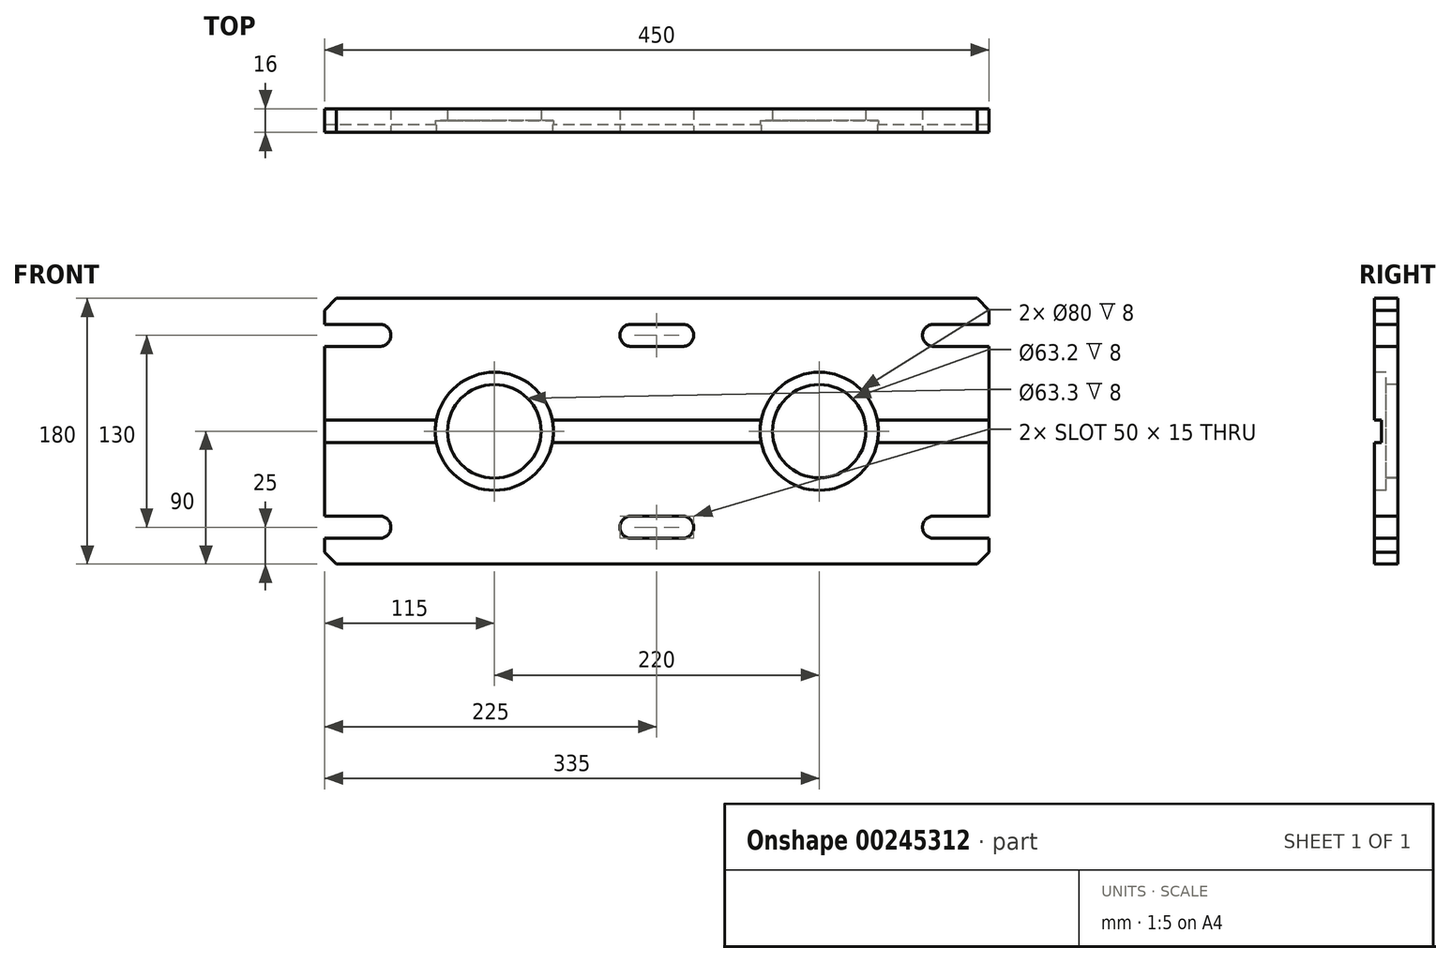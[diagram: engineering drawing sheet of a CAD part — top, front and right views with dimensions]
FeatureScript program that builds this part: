
annotation { "Feature Type Name" : "Feature", "Feature Type Description" : "" }
export const myFeature = defineFeature(function(context is Context, id is Id, definition is map)
    precondition{}
    {
        {
            var Q0;
            Q0=qCreatedBy(makeId("Front.planeOp"),FACE);
            var sketch = newSketch(context, id + "F0", { "sketchPlane" : qUnion([Q0])});
            skLineSegment(sketch, "E0.bottom", {"start": v(0, 0) * mm, "end": v(450, 0) * mm});
            skLineSegment(sketch, "E0.top", {"start": v(0, 180) * mm, "end": v(450, 180) * mm});
            skLineSegment(sketch, "E0.left", {"start": v(0, 0) * mm, "end": v(0, 180) * mm});
            skLineSegment(sketch, "E0.right", {"start": v(450, 0) * mm, "end": v(450, 180) * mm});
            skSolve(sketch);
        }
        {
            var Q0;
            Q0 = qSketchRegion(id + "F0", true);
            extrude(context, id + "F1", {"entities" : qUnion([Q0]), "depth" : 16 * mm, "offsetDistance" : 25 * mm});
        }
        {
            var Q0;
            Q0=makeQuery(id+"F1.opExtrude","SWEPT_EDGE",EDGE,{"disambiguationData":[OSD([sQuery(id+"F0.wireOp",EDGE,"E0.top"),sQuery(id+"F0.wireOp",EDGE,"E0.right")])]});
            var Q1;
            Q1=makeQuery(id+"F1.opExtrude","SWEPT_EDGE",EDGE,{"disambiguationData":[OSD([sQuery(id+"F0.wireOp",EDGE,"E0.bottom"),sQuery(id+"F0.wireOp",EDGE,"E0.right")])]});
            var Q2;
            Q2=makeQuery(id+"F1.opExtrude","SWEPT_EDGE",EDGE,{"disambiguationData":[OSD([sQuery(id+"F0.wireOp",EDGE,"E0.top"),sQuery(id+"F0.wireOp",EDGE,"E0.left")])]});
            var Q3;
            Q3=makeQuery(id+"F1.opExtrude","SWEPT_EDGE",EDGE,{"disambiguationData":[OSD([sQuery(id+"F0.wireOp",EDGE,"E0.bottom"),sQuery(id+"F0.wireOp",EDGE,"E0.left")])]});
            chamfer(context, id + "F2", {"entities" : qUnion([Q0, Q1, Q2, Q3]), "width" : 8 * mm, "tangentPropagation" : true});
        }
        {
            var Q0;
            Q0=makeQuery(id+"F1.opExtrude","CAP_FACE",FACE,{"disambiguationData":[OSD([sQuery(id+"F0.wireOp",EDGE,"E0.bottom"),sQuery(id+"F0.wireOp",EDGE,"E0.top"),sQuery(id+"F0.wireOp",EDGE,"E0.left"),sQuery(id+"F0.wireOp",EDGE,"E0.right")])],"isStart":false});
            var sketch = newSketch(context, id + "F3", { "sketchPlane" : qUnion([Q0])});
            skCircle(sketch, "E1", {"center": v(335, 90) * mm, "radius": 31.6 * mm});
            skPoint(sketch, "E1.centerSnap0", {"position": v(450, 90) * mm});
            skCircle(sketch, "E2", {"center": v(115, 90) * mm, "radius": 31.65 * mm});
            skPoint(sketch, "E2.centerSnap0", {"position": v(0, 90) * mm});
            skSolve(sketch);
        }
        {
            var Q0;
            Q0=makeQuery(id+"F3.imprint","IMPRINT",FACE,{"disambiguationData":[TD([[makeQuery(id+"F3.imprint","IMPRINT",EDGE,{"derivedFrom":sQuery(id+"F3.wireOp",EDGE,"E1")}),1.0]])]});
            var Q1;
            Q1=makeQuery(id+"F3.imprint","IMPRINT",FACE,{"disambiguationData":[TD([[makeQuery(id+"F3.imprint","IMPRINT",EDGE,{"derivedFrom":sQuery(id+"F3.wireOp",EDGE,"E2")}),1.0]])]});
            extrude(context, id + "F4", {"entities" : qUnion([Q0, Q1]), "operationType" : NewBodyOperationType.REMOVE, "endBound" : BoundingType.THROUGH_ALL, "oppositeDirection" : true, "depth" : 25 * mm, "offsetDistance" : 25 * mm});
        }
        {
            var Q0;
            Q0=makeQuery(id+"F1.opExtrude","CAP_FACE",FACE,{"disambiguationData":[OSD([sQuery(id+"F0.wireOp",EDGE,"E0.bottom"),sQuery(id+"F0.wireOp",EDGE,"E0.top"),sQuery(id+"F0.wireOp",EDGE,"E0.left"),sQuery(id+"F0.wireOp",EDGE,"E0.right")])],"isStart":false});
            var sketch = newSketch(context, id + "F5", { "sketchPlane" : qUnion([Q0])});
            skLineSegment(sketch, "E3.bottom", {"start": v(242.5, 147.5) * mm, "end": v(207.5, 147.5) * mm});
            skLineSegment(sketch, "E3.top", {"start": v(242.5, 162.5) * mm, "end": v(207.5, 162.5) * mm});
            skLineSegment(sketch, "E3.left", {"start": v(250, 155) * mm, "end": v(250, 155) * mm});
            skLineSegment(sketch, "E3.right", {"start": v(200, 155) * mm, "end": v(200, 155) * mm});
            skPoint(sketch, "E3.middle", {"position": v(225, 155) * mm});
            skPoint(sketch, "E3.middle.positionSnap0", {"position": v(225, 180) * mm});
            skPoint(sketch, "E3.centerSnap0", {"position": v(225, 180) * mm});
            skPoint(sketch, "E4.visualSharp", {"position": v(200, 162.5) * mm});
            skArc(sketch, "E4.filletArc", {"start": v(207.5, 162.5) * mm, "mid": v(202.2, 160.3) * mm, "end": v(200, 155) * mm});
            skPoint(sketch, "E5.visualSharp", {"position": v(200, 147.5) * mm});
            skArc(sketch, "E5.filletArc", {"start": v(200, 155) * mm, "mid": v(202.2, 149.7) * mm, "end": v(207.5, 147.5) * mm});
            skPoint(sketch, "E6.visualSharp", {"position": v(250, 147.5) * mm});
            skArc(sketch, "E6.filletArc", {"start": v(242.5, 147.5) * mm, "mid": v(247.8, 149.7) * mm, "end": v(250, 155) * mm});
            skPoint(sketch, "E7.visualSharp", {"position": v(250, 162.5) * mm});
            skArc(sketch, "E7.filletArc", {"start": v(250, 155) * mm, "mid": v(247.8, 160.3) * mm, "end": v(242.5, 162.5) * mm});
            skLineSegment(sketch, "E8.bottom", {"start": v(37.5, 147.5) * mm, "end": v(-68.92, 147.5) * mm});
            skLineSegment(sketch, "E8.top", {"start": v(37.5, 162.5) * mm, "end": v(-68.92, 162.5) * mm});
            skLineSegment(sketch, "E8.left", {"start": v(45, 155) * mm, "end": v(45, 155) * mm});
            skLineSegment(sketch, "E8.right", {"start": v(-68.92, 147.5) * mm, "end": v(-68.92, 162.5) * mm});
            skPoint(sketch, "E8.middle", {"position": v(-11.96, 155) * mm});
            skLineSegment(sketch, "E9.bottom", {"start": v(455.82, 162.5) * mm, "end": v(412.5, 162.5) * mm});
            skLineSegment(sketch, "E9.top", {"start": v(455.82, 147.5) * mm, "end": v(412.5, 147.5) * mm});
            skLineSegment(sketch, "E9.left", {"start": v(455.82, 162.5) * mm, "end": v(455.82, 147.5) * mm});
            skLineSegment(sketch, "E9.right", {"start": v(405, 155) * mm, "end": v(405, 155) * mm});
            skPoint(sketch, "E9.middle", {"position": v(430.4, 155) * mm});
            skPoint(sketch, "E10.visualSharp", {"position": v(45, 162.5) * mm});
            skArc(sketch, "E10.filletArc", {"start": v(45, 155) * mm, "mid": v(42.8, 160.3) * mm, "end": v(37.5, 162.5) * mm});
            skPoint(sketch, "E11.visualSharp", {"position": v(45, 147.5) * mm});
            skArc(sketch, "E11.filletArc", {"start": v(37.5, 147.5) * mm, "mid": v(42.8, 149.7) * mm, "end": v(45, 155) * mm});
            skPoint(sketch, "E12.visualSharp", {"position": v(405, 162.5) * mm});
            skArc(sketch, "E12.filletArc", {"start": v(412.5, 162.5) * mm, "mid": v(407.2, 160.3) * mm, "end": v(405, 155) * mm});
            skPoint(sketch, "E13.visualSharp", {"position": v(405, 147.5) * mm});
            skArc(sketch, "E13.filletArc", {"start": v(405, 155) * mm, "mid": v(407.2, 149.7) * mm, "end": v(412.5, 147.5) * mm});
            skLineSegment(sketch, "E14", {"start": v(0, 90) * mm, "end": v(450, 90) * mm, "construction": true});
            skArc(sketch, "E15.MirrorCS", {"start": v(200, 25) * mm, "mid": v(202.2, 30.3) * mm, "end": v(207.5, 32.5) * mm});
            skArc(sketch, "E16.MirrorCS", {"start": v(405, 25) * mm, "mid": v(407.2, 30.3) * mm, "end": v(412.5, 32.5) * mm});
            skArc(sketch, "E17.MirrorCS", {"start": v(45, 25) * mm, "mid": v(42.8, 19.7) * mm, "end": v(37.5, 17.5) * mm});
            skLineSegment(sketch, "E18.MirrorCS", {"start": v(455.82, 17.5) * mm, "end": v(455.82, 32.5) * mm});
            skLineSegment(sketch, "E19.MirrorCS", {"start": v(-68.92, 32.5) * mm, "end": v(-68.92, 17.5) * mm});
            skArc(sketch, "E20.MirrorCS", {"start": v(250, 25) * mm, "mid": v(247.8, 19.7) * mm, "end": v(242.5, 17.5) * mm});
            skArc(sketch, "E21.MirrorCS", {"start": v(242.5, 32.5) * mm, "mid": v(247.8, 30.3) * mm, "end": v(250, 25) * mm});
            skArc(sketch, "E22.MirrorCS", {"start": v(207.5, 17.5) * mm, "mid": v(202.2, 19.7) * mm, "end": v(200, 25) * mm});
            skArc(sketch, "E23.MirrorCS", {"start": v(412.5, 17.5) * mm, "mid": v(407.2, 19.7) * mm, "end": v(405, 25) * mm});
            skArc(sketch, "E24.MirrorCS", {"start": v(37.5, 32.5) * mm, "mid": v(42.8, 30.3) * mm, "end": v(45, 25) * mm});
            skLineSegment(sketch, "E25.MirrorCS", {"start": v(242.5, 17.5) * mm, "end": v(207.5, 17.5) * mm});
            skLineSegment(sketch, "E26.MirrorCS", {"start": v(242.5, 32.5) * mm, "end": v(207.5, 32.5) * mm});
            skPoint(sketch, "E27.MirrorP", {"position": v(225, 0) * mm});
            skLineSegment(sketch, "E28.MirrorCS", {"start": v(455.82, 32.5) * mm, "end": v(412.5, 32.5) * mm});
            skLineSegment(sketch, "E29.MirrorCS", {"start": v(455.82, 17.5) * mm, "end": v(412.5, 17.5) * mm});
            skLineSegment(sketch, "E30.MirrorCS", {"start": v(37.5, 17.5) * mm, "end": v(-68.92, 17.5) * mm});
            skPoint(sketch, "E31.MirrorP", {"position": v(225, 25) * mm});
            skLineSegment(sketch, "E32.MirrorCS", {"start": v(37.5, 32.5) * mm, "end": v(-68.92, 32.5) * mm});
            skPoint(sketch, "E33.MirrorP", {"position": v(45, 17.5) * mm});
            skLineSegment(sketch, "E34.MirrorCS", {"start": v(200, 25) * mm, "end": v(200, 25) * mm});
            skPoint(sketch, "E35.MirrorP", {"position": v(45, 32.5) * mm});
            skPoint(sketch, "E36.MirrorP", {"position": v(200, 17.5) * mm});
            skPoint(sketch, "E37.MirrorP", {"position": v(405, 32.5) * mm});
            skPoint(sketch, "E38.MirrorP", {"position": v(430.4, 25) * mm});
            skPoint(sketch, "E39.MirrorP", {"position": v(250, 17.5) * mm});
            skLineSegment(sketch, "E40.MirrorCS", {"start": v(250, 25) * mm, "end": v(250, 25) * mm});
            skPoint(sketch, "E41.MirrorP", {"position": v(200, 32.5) * mm});
            skPoint(sketch, "E42.MirrorP", {"position": v(-11.96, 25) * mm});
            skPoint(sketch, "E43.MirrorP", {"position": v(405, 17.5) * mm});
            skLineSegment(sketch, "E44.MirrorCS", {"start": v(405, 25) * mm, "end": v(405, 25) * mm});
            skLineSegment(sketch, "E45.MirrorCS", {"start": v(45, 25) * mm, "end": v(45, 25) * mm});
            skPoint(sketch, "E46.MirrorP", {"position": v(250, 32.5) * mm});
            skSolve(sketch);
        }
        {
            var Q0;
            Q0 = qSketchRegion(id + "F5", true);
            extrude(context, id + "F6", {"entities" : qUnion([Q0]), "operationType" : NewBodyOperationType.REMOVE, "endBound" : BoundingType.THROUGH_ALL, "oppositeDirection" : true, "depth" : 25 * mm, "offsetDistance" : 25 * mm});
        }
        {
            var Q0;
            Q0=makeQuery(id+"F1.opExtrude","CAP_FACE",FACE,{"disambiguationData":[OSD([sQuery(id+"F0.wireOp",EDGE,"E0.bottom"),sQuery(id+"F0.wireOp",EDGE,"E0.top"),sQuery(id+"F0.wireOp",EDGE,"E0.left"),sQuery(id+"F0.wireOp",EDGE,"E0.right")])],"isStart":false});
            var sketch = newSketch(context, id + "F7", { "sketchPlane" : qUnion([Q0])});
            skCircle(sketch, "E47", {"center": v(115, 90) * mm, "radius": 40 * mm});
            skSolve(sketch);
        }
        {
            var Q0;
            Q0=makeQuery(id+"F7.imprint","IMPRINT",FACE,{"disambiguationData":[TD([[makeQuery(id+"F7.imprint","IMPRINT",EDGE,{"derivedFrom":sQuery(id+"F7.wireOp",EDGE,"E47")}),1.0]])]});
            extrude(context, id + "F8", {"entities" : qUnion([Q0]), "operationType" : NewBodyOperationType.REMOVE, "oppositeDirection" : true, "depth" : 8 * mm, "offsetDistance" : 25 * mm});
        }
        {
            var Q0;
            Q0=makeQuery(id+"F1.opExtrude","CAP_FACE",FACE,{"disambiguationData":[OSD([sQuery(id+"F0.wireOp",EDGE,"E0.bottom"),sQuery(id+"F0.wireOp",EDGE,"E0.top"),sQuery(id+"F0.wireOp",EDGE,"E0.left"),sQuery(id+"F0.wireOp",EDGE,"E0.right")])],"isStart":false});
            var sketch = newSketch(context, id + "F9", { "sketchPlane" : qUnion([Q0])});
            skCircle(sketch, "E48", {"center": v(335, 90) * mm, "radius": 40 * mm});
            skSolve(sketch);
        }
        {
            var Q0;
            Q0 = qSketchRegion(id + "F9", true);
            extrude(context, id + "F10", {"entities" : qUnion([Q0]), "operationType" : NewBodyOperationType.REMOVE, "oppositeDirection" : true, "depth" : 8 * mm, "offsetDistance" : 25 * mm});
        }
        {
            var Q0;
            {var subQ1=sQuery(id+"F0.wireOp",EDGE,"E0.left");Q0=makeQuery(id+"F6.boolean.opBoolean","SPLIT",FACE,{"disambiguationData":[TD([makeQuery(id+"F6.opExtrude","SWEPT_FACE",FACE,{"disambiguationData":[OSD([sQuery(id+"F5.wireOp",EDGE,"E8.bottom")])]})])],"derivedFrom":makeQuery(id+"F1.opExtrude","SWEPT_FACE",FACE,{"disambiguationData":[OSD([subQ1])]})});}
            var sketch = newSketch(context, id + "F11", { "sketchPlane" : qUnion([Q0])});
            skLineSegment(sketch, "E49.bottom", {"start": v(21, 97.5) * mm, "end": v(11, 97.5) * mm});
            skLineSegment(sketch, "E49.top", {"start": v(21, 82.5) * mm, "end": v(11, 82.5) * mm});
            skLineSegment(sketch, "E49.left", {"start": v(21, 97.5) * mm, "end": v(21, 82.5) * mm});
            skLineSegment(sketch, "E49.right", {"start": v(11, 97.5) * mm, "end": v(11, 82.5) * mm});
            skPoint(sketch, "E49.middle", {"position": v(16, 90) * mm});
            skSolve(sketch);
        }
        {
            var Q0;
            Q0 = qSketchRegion(id + "F11", true);
            extrude(context, id + "F12", {"entities" : qUnion([Q0]), "operationType" : NewBodyOperationType.REMOVE, "endBound" : BoundingType.THROUGH_ALL, "oppositeDirection" : true, "depth" : 25 * mm, "offsetDistance" : 25 * mm});
        }
    });
